# Revit family: IS_iLifeS_T4588_BIM_GB
name_source: partatom
category: Plumbing Fixtures
units: mm (PartAtom-declared; Revit-internal decimal feet)

## family parameters
Always vertical = No
Cut with Voids When Loaded = No
OmniClass Number = 23.45.05.14.14
OmniClass Title = Sinks/Lavatories
Part Type = Normal
Room Calculation Point = No
Round Connector Dimension = Use Diameter
Shared = No
Work Plane-Based = No

## types (2) — shared parameters
Accessories = https://www.idealstandard.co.uk
AreaUnits = millimetres
AssetType = Fixed
BIMObjectName = IS_IdealStandard_Wall-hung washbasins_i.lifeS_T4588
BIMobject category = Wash Basins
BIMobject category code = wash-basins
BIMobject main category = Sanitary
BIMobject main category code = sanitary
Brand = Ideal Standard
Brand url = http://www.idealstandard.co.uk
Category = Sanitary
ConnectionType = Plumbing
CurrencyUnit = £
CurrentRevision = 1
Date of publishing = 27/05/2022
DurationUnit = Years
Edition number = 1
ElementType = Fixed
ExpectedLife = 99
Help = https://www.idealstandard.co.uk
IFC Classification = Sanitary Terminal
IfcExportAs = IfcSanitaryTerminalType
IfcExportType = TOILETPAN
Installation instructions = https://www.idealstandard.co.uk
InstallationInstructions = https://www.idealstandard.co.uk
LinearUnits = Millimetres
MaintenanceInformation = https://www.idealstandard.co.uk
Manufacturer = Ideal Standard
Manufacturer name = Ideal Standard
ManufacturerURL = https://www.idealstandard.co.uk
Material = Finefireclay
Material main = Finefireclay
ModelReference = i.life S Semicountertop washbasin 50 cm
NBS Reference Code = 45-35-70/369
NBS Reference Description = Wall hung wash basins
Name = Wall-hung washbasins_i.lifeS_T4588_IdealStandard
NettWeight = 10.64
NominalDepth = 359 mm
NominalHeight = 175 mm
NominalLength = 359 mm
NominalWidth = 499 mm
OmniClass Code = 23-11 21 21 13
OmniClass Description = Catch Basin
PredefinedType = Sanitary
Product Guid = b87eec6f-008a-43ea-91de-b216be20796d
Product SKU = T4588
Product certification = https://www.idealstandard.co.uk
Product data url = https://bimobject.com
Product family = I.life S
Product group = Saniatry: Basins
Product name = i.life S Semicountertop washbasin 50 cm
Product url = https://www.idealstandard.co.uk
ProductInformation = https://www.idealstandard.co.uk
QR code = http://bimobject.com
ReplacementCost = 0
Shape = Sculpture
Size = 360 x 175 x 500 mm
Space = Internal
SpareParts = https://www.idealstandard.co.uk
Technical description = https://www.idealstandard.co.uk
UNSPSC Code = 301815
URL = https://www.idealstandard.co.uk
Uniclass 2015 Code = Pr_40_20_96_96
Uniclass 2015 Name = Wall-hung washbasins
Uniclass2015Code = Pr_40_20_96_96
Uniclass2015Title = Wall-hung washbasins
Uniclass2015Version = v.25
Version = 1
VolumeUnits = Litres
WRASURL = https://www.wrasapprovals.co.uk
WarrantyDescription = manufacturer warranty
WarrantyDurationUnit = years
WashHandBasinMounting = Semicountertop Basin
WashHandBasinType = Semicountertop Basin
Youtube clip = https://www.youtube.com
zero-valued in all types: Cost

## per-type parameters (varying)
| type | BarCode | Color | Description | Features | Finish | GTIN code | MainColor | Model | ModelNumber |
| T458801 - i.life S Semicountertop washbasin 50 cm - White | 8014140491644 | White | Ideal Standard i.life S semicountertop 50 cm with 1 right hand taphole, overflow round; Fixing set E209167 incl., white, in carton box, EU pallet | semicountertop 50 cm with 1 right hand taphole, overflow round; Fixing set E209167 incl., white, in carton box, EU pallet | White | https://8014140491644 | White | T458801 | T458801 |
| T4588MA - i.life S Semicountertop washbasin 50 cm - Ideal Plus White | 8014140491651 | Ideal Plus White | Ideal Standard i.life S semicountertop 50 cm, 1 Right hand taphole, overflow round; Fixing set E209167 incl.; Ideal Plus, in carton box, EU pallet | semicountertop 50 cm, 1 Right hand taphole, overflow round; Fixing set E209167 incl.; Ideal Plus, in carton box, EU pallet | Ideal Plus White | https://8014140491651 | Ideal Plus White | T4588MA | T4588MA |

## geometry (parser evidence)
native form markers: Sweep x2
no freeform markers — native parametric forms only
